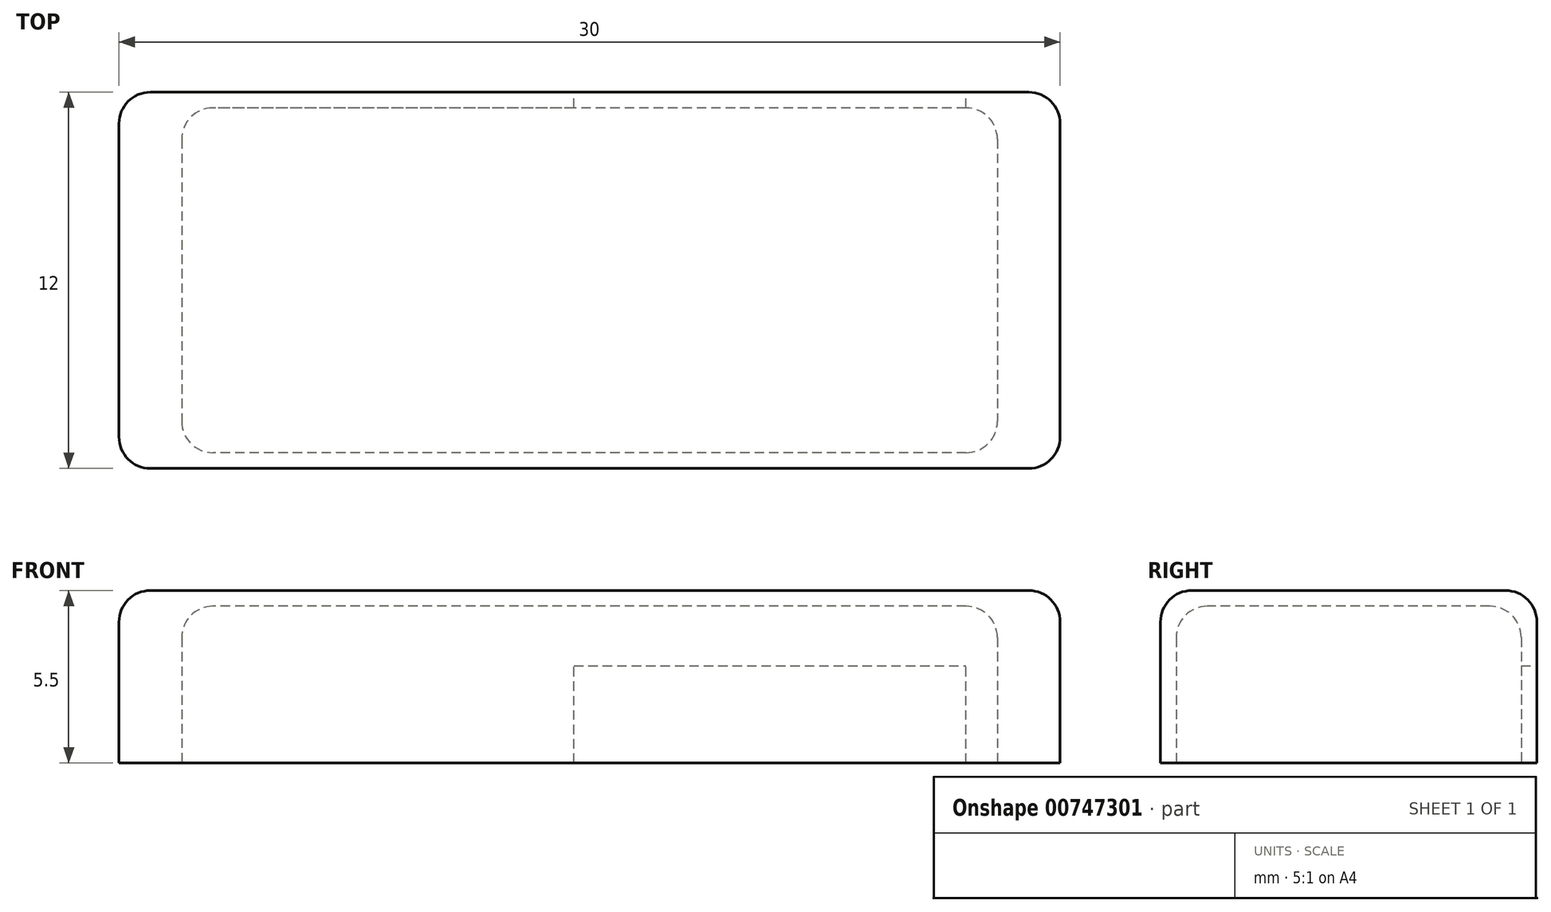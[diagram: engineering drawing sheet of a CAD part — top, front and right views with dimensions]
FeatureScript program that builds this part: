
annotation { "Feature Type Name" : "Feature", "Feature Type Description" : "" }
export const myFeature = defineFeature(function(context is Context, id is Id, definition is map)
    precondition{}
    {
        {
            var Q0;
            Q0=qCreatedBy(makeId("Top.planeOp"),FACE);
            var sketch = newSketch(context, id + "F0", { "sketchPlane" : qUnion([Q0])});
            skLineSegment(sketch, "E0.bottom", {"start": v(1, 2.88) * mm, "end": v(29, 2.88) * mm});
            skLineSegment(sketch, "E0.top", {"start": v(1, 14.88) * mm, "end": v(29, 14.88) * mm});
            skLineSegment(sketch, "E0.left", {"start": v(0, 3.88) * mm, "end": v(0, 13.88) * mm});
            skLineSegment(sketch, "E0.right", {"start": v(30, 3.88) * mm, "end": v(30, 13.88) * mm});
            skPoint(sketch, "E1.visualSharp", {"position": v(0, 14.88) * mm});
            skArc(sketch, "E1.filletArc", {"start": v(1, 14.88) * mm, "mid": v(0.3, 14.58) * mm, "end": v(0, 13.88) * mm});
            skPoint(sketch, "E2.visualSharp", {"position": v(30, 14.88) * mm});
            skArc(sketch, "E2.filletArc", {"start": v(30, 13.88) * mm, "mid": v(29.7, 14.58) * mm, "end": v(29, 14.88) * mm});
            skPoint(sketch, "E3.visualSharp", {"position": v(30, 2.88) * mm});
            skArc(sketch, "E3.filletArc", {"start": v(29, 2.88) * mm, "mid": v(29.7, 3.17) * mm, "end": v(30, 3.88) * mm});
            skPoint(sketch, "E4.visualSharp", {"position": v(0, 2.88) * mm});
            skArc(sketch, "E4.filletArc", {"start": v(0, 3.88) * mm, "mid": v(0.3, 3.17) * mm, "end": v(1, 2.88) * mm});
            skSolve(sketch);
        }
        {
            var Q0;
            Q0=qSketchRegion(id+"F0",true);
            extrude(context, id + "F1", {"entities" : qUnion([Q0]), "depth" : 5.5 * mm, "offsetDistance" : 25 * mm});
        }
        {
            var Q0;
            Q0=makeQuery(id+"F1.opExtrude","CAP_FACE",FACE,{"disambiguationData":[OSD([sQuery(id+"F0.wireOp",EDGE,"E0.bottom"),sQuery(id+"F0.wireOp",EDGE,"E0.top"),sQuery(id+"F0.wireOp",EDGE,"E0.left"),sQuery(id+"F0.wireOp",EDGE,"E0.right")])],"isStart":false});
            fillet(context, id + "F2", {"entities" : qUnion([Q0]), "radius" : 1 * mm, "tangentPropagation" : true, "allowEdgeOverflow" : false});
        }
        {
            var Q0;
            Q0=qCreatedBy(makeId("Top.planeOp"),FACE);
            var sketch = newSketch(context, id + "F3", { "sketchPlane" : qUnion([Q0])});
            skLineSegment(sketch, "E5.bottom", {"start": v(27, 14.38) * mm, "end": v(3, 14.38) * mm});
            skLineSegment(sketch, "E5.top", {"start": v(27, 3.38) * mm, "end": v(3, 3.38) * mm});
            skLineSegment(sketch, "E5.left", {"start": v(28, 13.38) * mm, "end": v(28, 4.38) * mm});
            skLineSegment(sketch, "E5.right", {"start": v(2, 13.38) * mm, "end": v(2, 4.38) * mm});
            skLineSegment(sketch, "E6.bottom", {"start": v(14.5, 3.38) * mm, "end": v(27, 3.38) * mm});
            skPoint(sketch, "E7.visualSharp", {"position": v(2, 3.38) * mm});
            skArc(sketch, "E7.filletArc", {"start": v(2, 4.38) * mm, "mid": v(2.3, 3.67) * mm, "end": v(3, 3.38) * mm});
            skPoint(sketch, "E8.visualSharp", {"position": v(2, 14.38) * mm});
            skArc(sketch, "E8.filletArc", {"start": v(3, 14.38) * mm, "mid": v(2.3, 14.08) * mm, "end": v(2, 13.38) * mm});
            skPoint(sketch, "E9.visualSharp", {"position": v(28, 14.38) * mm});
            skArc(sketch, "E9.filletArc", {"start": v(28, 13.38) * mm, "mid": v(27.7, 14.08) * mm, "end": v(27, 14.38) * mm});
            skPoint(sketch, "E10.visualSharp", {"position": v(28, 3.38) * mm});
            skArc(sketch, "E10.filletArc", {"start": v(27, 3.38) * mm, "mid": v(27.7, 3.67) * mm, "end": v(28, 4.38) * mm});
            skSolve(sketch);
        }
        {
            var Q0;
            Q0=qSketchRegion(id+"F3",true);
            extrude(context, id + "F4", {"entities" : qUnion([Q0]), "operationType" : NewBodyOperationType.REMOVE, "depth" : 5 * mm, "offsetDistance" : 25 * mm});
        }
        {
            var Q0;
            Q0=qCreatedBy(makeId("Top.planeOp"),FACE);
            var sketch = newSketch(context, id + "F5", { "sketchPlane" : qUnion([Q0])});
            skLineSegment(sketch, "E11.bottom", {"start": v(14.5, 13.29) * mm, "end": v(27, 13.29) * mm});
            skLineSegment(sketch, "E11.top", {"start": v(14.5, 16.27) * mm, "end": v(27, 16.27) * mm});
            skLineSegment(sketch, "E11.left", {"start": v(14.5, 13.29) * mm, "end": v(14.5, 16.27) * mm});
            skLineSegment(sketch, "E11.right", {"start": v(27, 13.29) * mm, "end": v(27, 16.27) * mm});
            skSolve(sketch);
        }
        {
            var Q0;
            Q0=qSketchRegion(id+"F5",true);
            extrude(context, id + "F6", {"entities" : qUnion([Q0]), "operationType" : NewBodyOperationType.REMOVE, "depth" : 3.1 * mm, "offsetDistance" : 25 * mm});
        }
        {
            var Q0;
            Q0=makeQuery(id+"F4.boolean.opBoolean","COPY",EDGE,{"derivedFrom":makeQuery(id+"F4.opExtrude","CAP_EDGE",EDGE,{"disambiguationData":[OSD([sQuery(id+"F3.wireOp",EDGE,"E5.top"),sQuery(id+"F3.wireOp",EDGE,"E6.bottom")])],"isStart":false})});
            var Q1;
            Q1=makeQuery(id+"F4.boolean.opBoolean","COPY",EDGE,{"derivedFrom":makeQuery(id+"F4.opExtrude","CAP_EDGE",EDGE,{"disambiguationData":[OSD([sQuery(id+"F3.wireOp",EDGE,"E5.left")])],"isStart":false})});
            var Q2;
            Q2=makeQuery(id+"F4.boolean.opBoolean","COPY",EDGE,{"derivedFrom":makeQuery(id+"F4.opExtrude","CAP_EDGE",EDGE,{"disambiguationData":[OSD([sQuery(id+"F3.wireOp",EDGE,"E7.filletArc")])],"isStart":false})});
            var Q3;
            Q3=makeQuery(id+"F4.boolean.opBoolean","COPY",EDGE,{"derivedFrom":makeQuery(id+"F4.opExtrude","CAP_EDGE",EDGE,{"disambiguationData":[OSD([sQuery(id+"F3.wireOp",EDGE,"E5.right")])],"isStart":false})});
            var Q4;
            Q4=makeQuery(id+"F4.boolean.opBoolean","COPY",EDGE,{"derivedFrom":makeQuery(id+"F4.opExtrude","CAP_EDGE",EDGE,{"disambiguationData":[OSD([sQuery(id+"F3.wireOp",EDGE,"E5.bottom")])],"isStart":false})});
            var Q5;
            Q5=makeQuery(id+"F4.boolean.opBoolean","COPY",EDGE,{"derivedFrom":makeQuery(id+"F4.opExtrude","CAP_EDGE",EDGE,{"disambiguationData":[OSD([sQuery(id+"F3.wireOp",EDGE,"E8.filletArc")])],"isStart":false})});
            var Q6;
            Q6=makeQuery(id+"F4.boolean.opBoolean","COPY",EDGE,{"derivedFrom":makeQuery(id+"F4.opExtrude","CAP_EDGE",EDGE,{"disambiguationData":[OSD([sQuery(id+"F3.wireOp",EDGE,"E9.filletArc")])],"isStart":false})});
            var Q7;
            Q7=makeQuery(id+"F4.boolean.opBoolean","COPY",EDGE,{"derivedFrom":makeQuery(id+"F4.opExtrude","CAP_EDGE",EDGE,{"disambiguationData":[OSD([sQuery(id+"F3.wireOp",EDGE,"E10.filletArc")])],"isStart":false})});
            fillet(context, id + "F7", {"entities" : qUnion([Q0, Q1, Q2, Q3, Q4, Q5, Q6, Q7]), "radius" : 1 * mm, "tangentPropagation" : true, "allowEdgeOverflow" : false});
        }
    });
